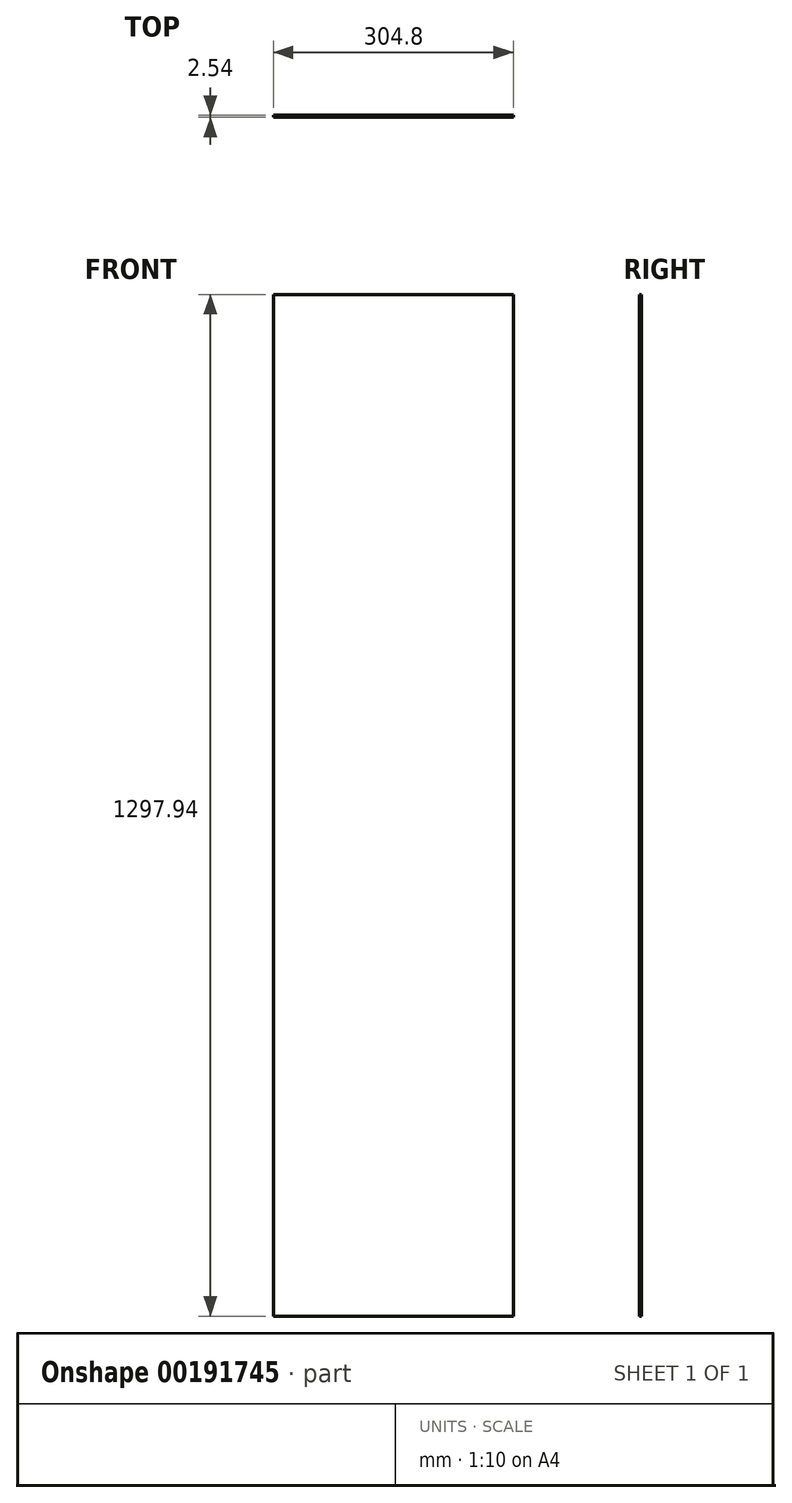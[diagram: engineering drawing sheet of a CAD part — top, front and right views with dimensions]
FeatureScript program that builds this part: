
annotation { "Feature Type Name" : "Feature", "Feature Type Description" : "" }
export const myFeature = defineFeature(function(context is Context, id is Id, definition is map)
    precondition{}
    {
        {
            var Q0;
            Q0=qCreatedBy(makeId("Front.planeOp"),FACE);
            var sketch = newSketch(context, id + "F0", { "sketchPlane" : qUnion([Q0])});
            skLineSegment(sketch, "E0.bottom", {"start": v(-361.17, 666.32) * mm, "end": v(-56.37, 666.32) * mm});
            skLineSegment(sketch, "E0.top", {"start": v(-361.17, -631.62) * mm, "end": v(-56.37, -631.62) * mm});
            skLineSegment(sketch, "E0.left", {"start": v(-361.17, 666.32) * mm, "end": v(-361.17, -631.62) * mm});
            skLineSegment(sketch, "E0.right", {"start": v(-56.37, 666.32) * mm, "end": v(-56.37, -631.62) * mm});
            skSolve(sketch);
        }
        {
            var Q0;
            Q0 = qSketchRegion(id + "F0", true);
            var Q1;
            Q1=makeQuery(id+"F0.imprint","IMPRINT",FACE,{"disambiguationData":[TD([[makeQuery(id+"F0.imprint","IMPRINT",EDGE,{"derivedFrom":sQuery(id+"F0.wireOp",EDGE,"E0.bottom")}),-1.0]])]});
            extrude(context, id + "F1", {"entities" : qUnion([Q0, Q1]), "depth" : 2.54 * mm});
        }
    });
